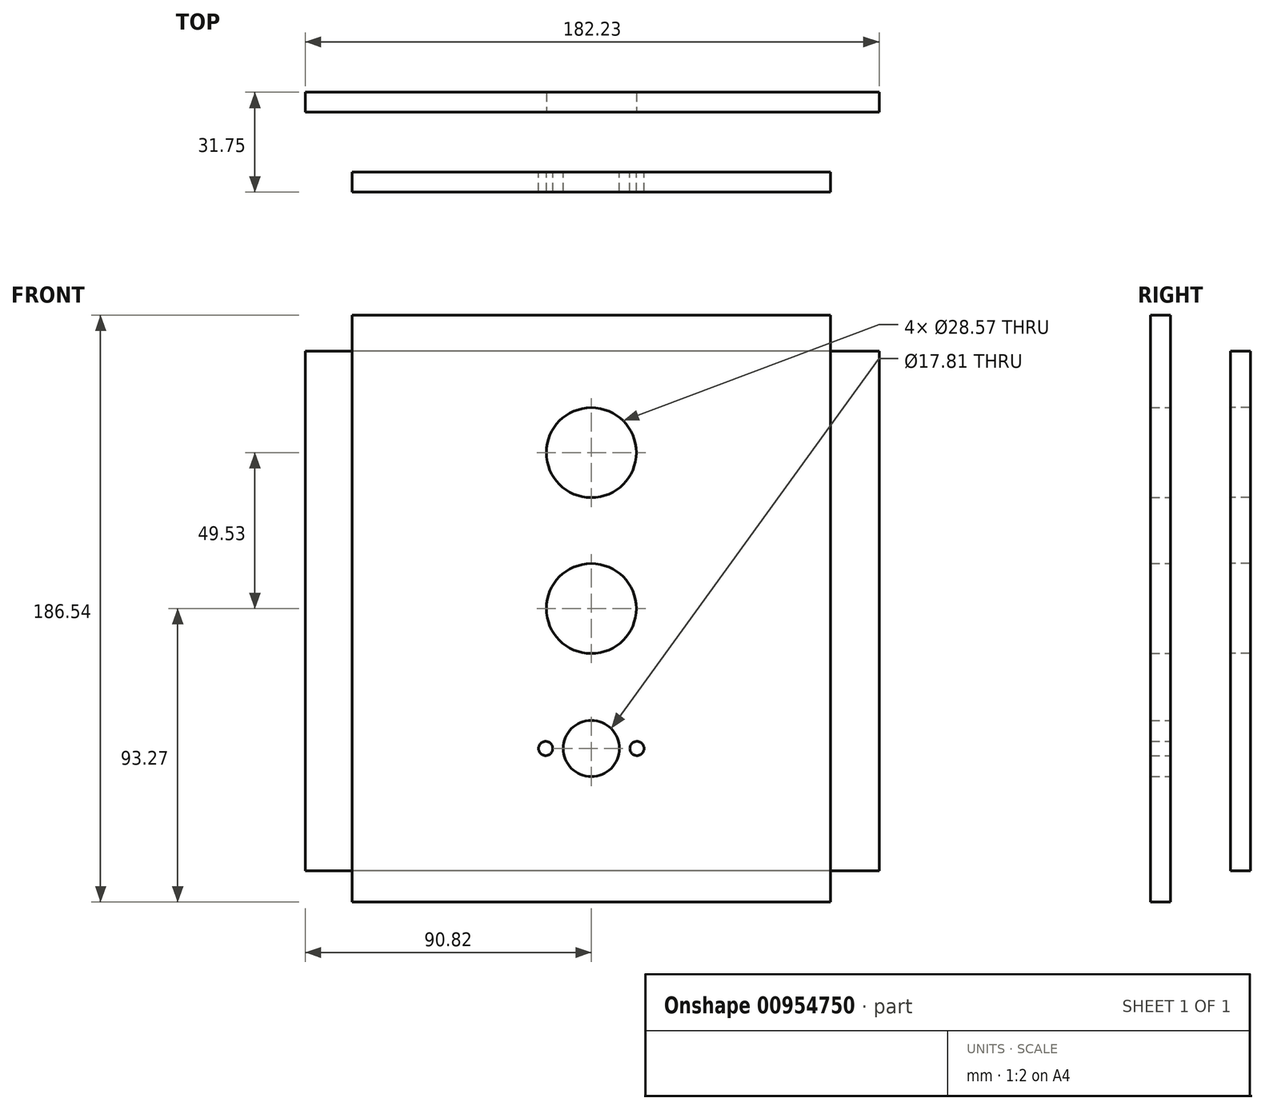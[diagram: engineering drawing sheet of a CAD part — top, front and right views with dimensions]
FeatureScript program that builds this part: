
annotation { "Feature Type Name" : "Feature", "Feature Type Description" : "" }
export const myFeature = defineFeature(function(context is Context, id is Id, definition is map)
    precondition{}
    {
        {
            var Q0;
            Q0=qCreatedBy(makeId("Front.planeOp"),FACE);
            var sketch = newSketch(context, id + "F0", { "sketchPlane" : qUnion([Q0])});
            skCircle(sketch, "E0", {"center": v(0, 0) * mm, "radius": 14.29 * mm});
            skLineSegment(sketch, "E1", {"start": v(0, 0) * mm, "end": v(0, -44.45) * mm, "construction": true});
            skCircle(sketch, "E2", {"center": v(0, -44.45) * mm, "radius": 8.9 * mm});
            skLineSegment(sketch, "E3.bottom", {"start": v(-75.9, 93.27) * mm, "end": v(75.9, 93.27) * mm});
            skLineSegment(sketch, "E3.top", {"start": v(-75.9, -93.27) * mm, "end": v(75.9, -93.27) * mm});
            skLineSegment(sketch, "E3.left", {"start": v(-75.9, 93.27) * mm, "end": v(-75.9, -93.27) * mm});
            skLineSegment(sketch, "E3.right", {"start": v(75.9, 93.27) * mm, "end": v(75.9, -93.27) * mm});
            skLineSegment(sketch, "E4", {"start": v(0, 0) * mm, "end": v(0, -93.27) * mm, "construction": true});
            skLineSegment(sketch, "E5", {"start": v(0, 0) * mm, "end": v(75.9, 0) * mm, "construction": true});
            skLineSegment(sketch, "E6", {"start": v(0, -44.45) * mm, "end": v(-14.5, -44.45) * mm, "construction": true});
            skLineSegment(sketch, "E7", {"start": v(0, -44.45) * mm, "end": v(14.5, -44.45) * mm, "construction": true});
            skCircle(sketch, "E8", {"center": v(0, 49.53) * mm, "radius": 14.29 * mm});
            skLineSegment(sketch, "E9", {"start": v(0, 49.53) * mm, "end": v(0, 0) * mm, "construction": true});
            skSolve(sketch);
        }
        {
            var Q0;
            Q0=makeQuery(id+"F0.imprint","IMPRINT",FACE,{"disambiguationData":[TD([[makeQuery(id+"F0.imprint","IMPRINT",EDGE,{"derivedFrom":sQuery(id+"F0.wireOp",EDGE,"E0")}),-1.0]])]});
            var Q1;
            Q1=makeQuery(id+"F0.imprint","IMPRINT",FACE,{"disambiguationData":[TD([[makeQuery(id+"F0.imprint","IMPRINT",EDGE,{"derivedFrom":sQuery(id+"F0.wireOp",EDGE,"E2")}),1.0]])]});
            extrude(context, id + "F1", {"entities" : qUnion([Q0, Q1]), "depth" : 6.35 * mm, "offsetDistance" : 25.4 * mm});
        }
        {
            var Q0;
            Q0=makeQuery(id+"F0.imprint","IMPRINT",FACE,{"disambiguationData":[TD([[makeQuery(id+"F0.imprint","IMPRINT",EDGE,{"derivedFrom":sQuery(id+"F0.wireOp",EDGE,"E2")}),1.0]])]});
            extrude(context, id + "F2", {"entities" : qUnion([Q0]), "operationType" : NewBodyOperationType.REMOVE, "endBound" : BoundingType.THROUGH_ALL, "depth" : 25.4 * mm, "offsetDistance" : 25.4 * mm});
        }
        {
            var Q0;
            Q0=sQuery(id+"F0.wireOp",VERTEX,"E6.end");
            var Q1;
            Q1=sQuery(id+"F0.wireOp",VERTEX,"E7.end");
            var Q2;
            Q2=makeQuery(id+"F1.opExtrude","SWEPT_BODY",BODY,{"disambiguationData":[OSD([sQuery(id+"F0.wireOp",EDGE,"E0"),sQuery(id+"F0.wireOp",EDGE,"E2"),sQuery(id+"F0.wireOp",EDGE,"E3.bottom"),sQuery(id+"F0.wireOp",EDGE,"E3.top"),sQuery(id+"F0.wireOp",EDGE,"E3.left"),sQuery(id+"F0.wireOp",EDGE,"E3.right")])]});
            hole(context, id + "F3", {"style" : HoleStyle.SIMPLE, "endStyle" : HoleEndStyle.THROUGH, "oppositeDirection" : true, "standardTappedOrClearance" : lookupTablePath({ "fit" : "Normal", "standard" : "ISO", "size" : "M4", "type" : "Clearance" }), "standardBlindInLast" : lookupTablePath({ "fit" : "Normal", "standard" : "ISO", "engagement" : "75%", "pitch" : "0.7 mm", "size" : "M4", "type" : "Clearance & tapped" }), "holeDiameter" : 4.5 * mm, "majorDiameter" : 6.35 * mm, "isTappedThrough" : true, "tappedDepth" : 12.7 * mm, "tapClearance" : 3, "locations" : qUnion([Q0, Q1]), "scope" : qUnion([Q2])});
        }
        {
            var Q0;
            Q0=makeQuery(id+"F0.imprint","IMPRINT",FACE,{"disambiguationData":[TD([[makeQuery(id+"F0.imprint","IMPRINT",EDGE,{"derivedFrom":sQuery(id+"F0.wireOp",EDGE,"E0")}),-1.0]])]});
            cPlane(context, id + "F4", {"entities" : qUnion([Q0]), "cplaneType" : CPlaneType.OFFSET, "offset" : 19.05 * mm, "oppositeDirection" : true, "width" : 152.4 * mm, "height" : 152.4 * mm});
        }
        {
            var Q0;
            Q0=qCreatedBy(id+"F4.planeOp",FACE);
            var sketch = newSketch(context, id + "F5", { "sketchPlane" : qUnion([Q0])});
            skCircle(sketch, "E10.0", {"center": v(0, 0) * mm, "radius": 14.29 * mm});
            skCircle(sketch, "E11", {"center": v(0, 49.53) * mm, "radius": 14.29 * mm});
            skLineSegment(sketch, "E12", {"start": v(0, 0) * mm, "end": v(0, 49.53) * mm, "construction": true});
            skLineSegment(sketch, "E13.bottom", {"start": v(91.41, 81.75) * mm, "end": v(-90.82, 81.75) * mm});
            skLineSegment(sketch, "E13.top", {"start": v(91.41, -83.36) * mm, "end": v(-90.82, -83.36) * mm});
            skLineSegment(sketch, "E13.left", {"start": v(91.41, 81.75) * mm, "end": v(91.41, -83.36) * mm});
            skLineSegment(sketch, "E13.right", {"start": v(-90.82, 81.75) * mm, "end": v(-90.82, -83.36) * mm});
            skSolve(sketch);
        }
        {
            var Q0;
            Q0 = qSketchRegion(id + "F5", true);
            extrude(context, id + "F6", {"entities" : qUnion([Q0]), "oppositeDirection" : true, "depth" : 6.35 * mm, "offsetDistance" : 25.4 * mm});
        }
    });
